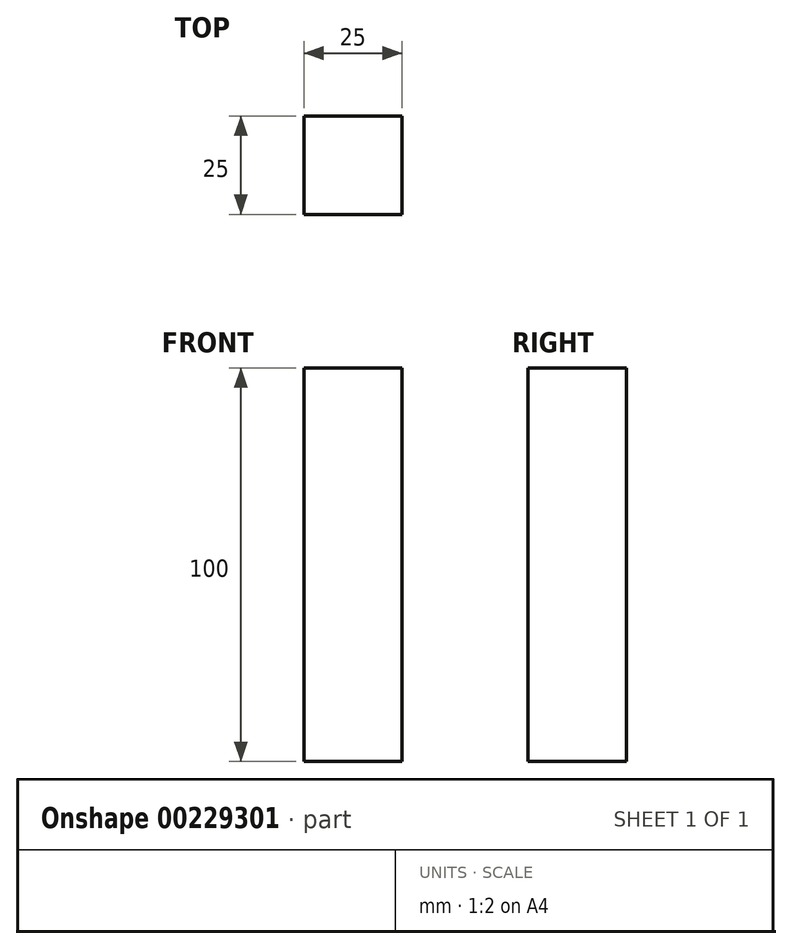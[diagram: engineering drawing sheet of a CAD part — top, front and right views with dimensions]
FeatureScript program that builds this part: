
annotation { "Feature Type Name" : "Feature", "Feature Type Description" : "" }
export const myFeature = defineFeature(function(context is Context, id is Id, definition is map)
    precondition{}
    {
        {
            var Q0;
            Q0=qCreatedBy(makeId("Top.planeOp"),FACE);
            var sketch = newSketch(context, id + "F0", { "sketchPlane" : qUnion([Q0])});
            skLineSegment(sketch, "E0.bottom", {"start": v(-12.5, 12.5) * mm, "end": v(12.5, 12.5) * mm});
            skLineSegment(sketch, "E0.top", {"start": v(-12.5, -12.5) * mm, "end": v(12.5, -12.5) * mm});
            skLineSegment(sketch, "E0.left", {"start": v(-12.5, 12.5) * mm, "end": v(-12.5, -12.5) * mm});
            skLineSegment(sketch, "E0.right", {"start": v(12.5, 12.5) * mm, "end": v(12.5, -12.5) * mm});
            skSolve(sketch);
        }
        {
            var Q0;
            Q0=makeQuery(id+"F0.imprint","IMPRINT",FACE,{"disambiguationData":[TD([[makeQuery(id+"F0.imprint","IMPRINT",EDGE,{"derivedFrom":sQuery(id+"F0.wireOp",EDGE,"E0.bottom")}),-1.0]])]});
            extrude(context, id + "F1", {"entities" : qUnion([Q0]), "depth" : 100 * mm});
        }
    });
